# Revit family: pd-rp40_160ga17_60Hz_モデル修正
name_source: partatom
category: 機械設備
units: mm (PartAtom-declared; Revit-internal decimal feet)

## family parameters
OmniClass タイトル = Split System Air Conditioning Units
OmniClass 番号 = 23.75.10.24.21.27.27
パーツ タイプ = 標準
ロード時にボイドで切り取り = いいえ
丸型コネクタ寸法 = 直径を使用
作業面ベース = いいえ
共有 = いいえ
常に垂直 = いいえ
部屋計算ポイント = はい

## types (9) — shared parameters
Depth = 701  [stored 2.29987 ft]
Height = 272
IfcExportAs = IfcUnitaryEquipmentType
IfcExportType = AIRCONDITIONINGUNIT
OmniClassCode = 23-33 17 13 11
URL = https://www.mitsubishielectric.co.jp
Uniclass2015Code = Pr_70_65_03_84
Uniclass2015Title = Split coil remote air cooled condensing units
Uniclass2015Version = Systems v1.9
ダクト高 = 178 mm
ドレン管径 = 32.00 mm
パネルマテリアル = <カテゴリ別>
仕様書バージョン = Version1.0
企業コード = 108420
冷媒管径 = 100.00 mm
冷媒高低圧ガス管径 = 0.00 mm
分類コード = 50053003123050
加湿給水管径 = 0.00 mm
参照している仕様書等のバージョン = 公共建築工事標準仕様書（機械設備工事編）平成31年度版
周波数 = 60 Hz
呼称 = 室内機_天井吊(隠ぺい)形(⽚ダクト形)
始動方式 = 直入
形式 = 天井吊（隠ぺい）形（片ダクト形）
本体マテリアル = <カテゴリ別>
極数 = 3
機外静圧 = 10.0 Pa
法定耐用年数 = 15
消費電力_加湿器 = 0 W
消費電力_電気ヒーター = 0 W
相 = 1
相_電気ヒーター = 1
積算_科目 = 1 空気調和設備
符号 = PAC-CIS
製品リリース年月 = 2021年5月10日
製品出荷対象 = 国内
製造元 = 三菱電機株式会社
設置方法 = 天井吊(隠ぺい)形
説明 = 店舗・事務所用パッケージエアコン(Mr.SLIM) 天井ビルトイン形
負荷分類 = 3_ファン類
運転質量 = 0.00 kg
電圧 = 200 V
電圧_電気ヒーター = 0 V
zero-valued in all types: 価格, 新鮮空気取入口, 有効加湿量

## per-type parameters (varying)
| type | MAX風量 | MID風量 | MIN風量 | Width | ダクト幅 | 冷媒ガス管径 | 冷媒液管径 | 冷媒管径符号 | 冷房能力 | 暖房能力 | 消費電力 | 消費電力_冷房 | 消費電力_暖房 | 製品質量 | 質量 | 電動機出力_送風機 | 音響パワーレベル(dB) | 風量 | 風量（m3／min） | 風量（中）（m3／min） | 風量（弱）（m3／min） | 騒音レベル（中）(dB) | 騒音レベル（弱）(dB) |
| PD-RP40GA17 | 840.0 m³/h | 720.0 m³/h | 600.0 m³/h | 900  [stored 2.95276 ft] | 860 mm | 12.70 mm | 6.35 mm | Ac | 3600 W | 4000 W | 100 W | 100 W | 100 W | 29.00 kg | 34.80 kg | 85 W | 58 | 840.0 m³/h | 14 | 12 | 10 | 55 | 52 |
| PD-RP50GA17 | 840.0 m³/h | 720.0 m³/h | 600.0 m³/h | 900  [stored 2.95276 ft] | 860 mm | 12.70 mm | 6.35 mm | Ac | 4500 W | 5000 W | 100 W | 100 W | 100 W | 29.00 kg | 34.80 kg | 85 W | 59 | 840.0 m³/h | 14 | 12 | 10 | 55 | 53 |
| PD-RP56GA17 | 840.0 m³/h | 720.0 m³/h | 600.0 m³/h | 900  [stored 2.95276 ft] | 860 mm | 12.70 mm | 6.35 mm | Ac | 5000 W | 5600 W | 100 W | 100 W | 100 W | 29.00 kg | 34.80 kg | 85 W | 59 | 840.0 m³/h | 14 | 12 | 10 | 56 | 53 |
| PD-RP63GA17 | 1140.0 m³/h | 960.0 m³/h | 780.0 m³/h | 1100 | 1060 mm | 12.70 mm | 6.35 mm | Ac | 5600 W | 6300 W | 100 W | 100 W | 100 W | 33.00 kg | 39.60 kg | 121 W | 60 | 1140.0 m³/h | 19 | 16 | 13 | 57 | 54 |
| PD-RP71GA17 | 1140.0 m³/h | 960.0 m³/h | 780.0 m³/h | 1100 | 1060 mm | 15.88 mm | 9.52 mm | Bd | 6300 W | 7000 W | 100 W | 100 W | 100 W | 33.00 kg | 39.60 kg | 121 W | 60 | 1140.0 m³/h | 19 | 16 | 13 | 57 | 55 |
| PD-RP80GA17 | 1140.0 m³/h | 960.0 m³/h | 780.0 m³/h | 1100 | 1060 mm | 15.88 mm | 9.52 mm | Bd | 7100 W | 8000 W | 100 W | 100 W | 100 W | 33.00 kg | 39.60 kg | 121 W | 60 | 1140.0 m³/h | 19 | 16 | 13 | 57 | 56 |
| PD-RP112GA17 | 1680.0 m³/h | 1440.0 m³/h | 1200.0 m³/h | 1400  [stored 4.59318 ft] | 1360 mm | 15.88 mm | 9.52 mm | Bd | 10000 W | 11200 W | 190 W | 190 W | 190 W | 42.00 kg | 50.40 kg | 244 W | 62 | 1680.0 m³/h | 28 | 24 | 20 | 60 | 59 |
| PD-RP140GA17 | 1860.0 m³/h | 1560.0 m³/h | 1320.0 m³/h | 1400  [stored 4.59318 ft] | 1360 mm | 15.88 mm | 9.52 mm | Bd | 12500 W | 14000 W | 220 W | 220 W | 220 W | 42.00 kg | 50.40 kg | 244 W | 64 | 1860.0 m³/h | 31 | 26 | 22 | 62 | 61 |
| PD-RP160GA17 | 2040.0 m³/h | 1740.0 m³/h | 1440.0 m³/h | 1400  [stored 4.59318 ft] | 1360 mm | 15.88 mm | 9.52 mm | Bd | 14000 W | 16000 W | 260 W | 260 W | 260 W | 42.00 kg | 50.40 kg | 244 W | 67 | 2040.0 m³/h | 34 | 29 | 24 | 65 | 63 |

note: column(s) folded — value = type name in every type: モデル

note: [stored X ft] marks values corroborated as IEEE doubles in the binary element streams (Revit-internal decimal feet)
